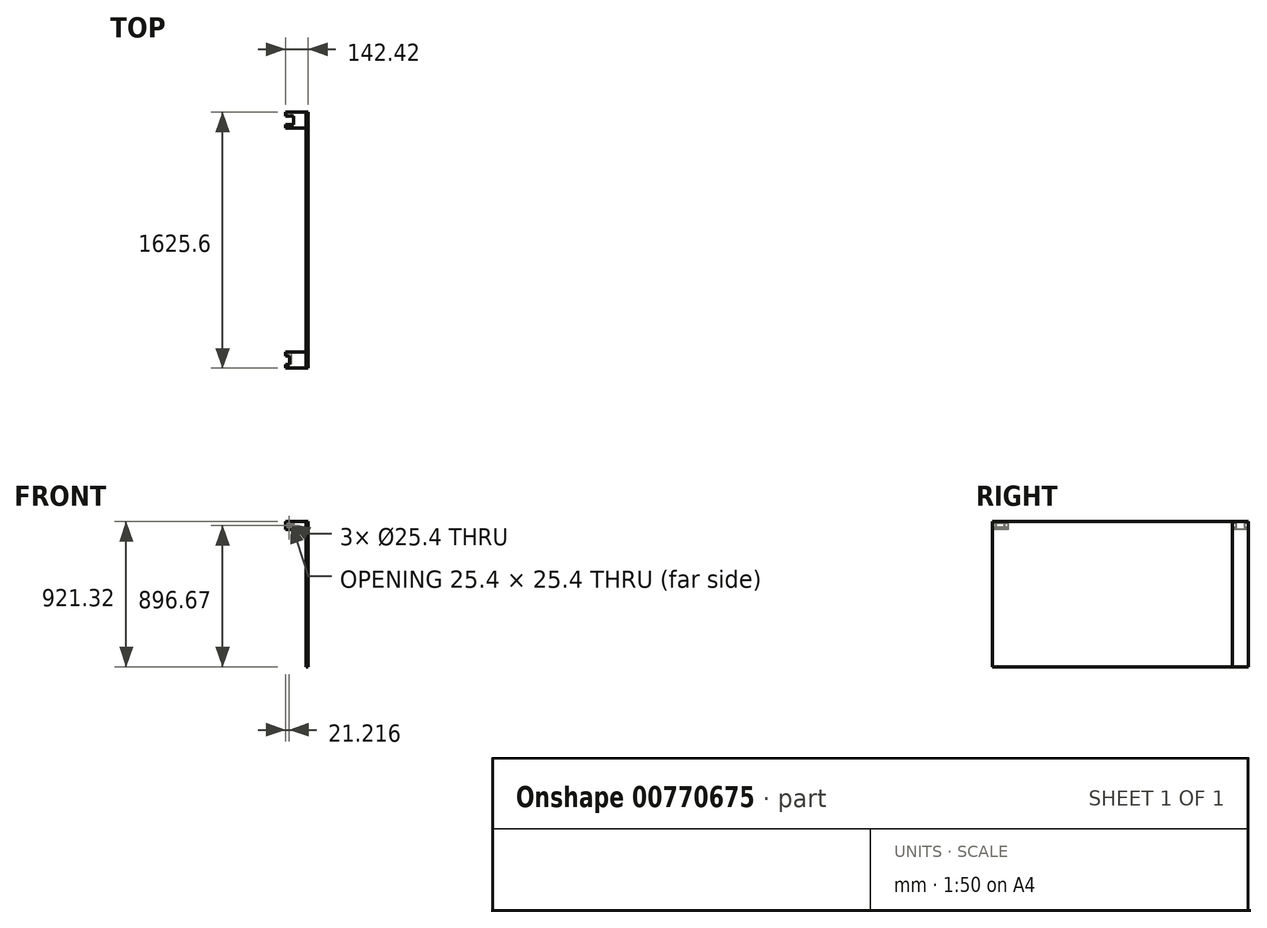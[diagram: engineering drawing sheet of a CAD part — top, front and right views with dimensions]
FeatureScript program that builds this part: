
annotation { "Feature Type Name" : "Feature", "Feature Type Description" : "" }
export const myFeature = defineFeature(function(context is Context, id is Id, definition is map)
    precondition{}
    {
        {
            var Q0;
            Q0=qCreatedBy(makeId("Front.planeOp"),FACE);
            var sketch = newSketch(context, id + "F0", { "sketchPlane" : qUnion([Q0])});
            skLineSegment(sketch, "E0.bottom", {"start": v(0, 0) * mm, "end": v(131.22, 0) * mm});
            skLineSegment(sketch, "E0.top", {"start": v(0, 48.37) * mm, "end": v(131.22, 48.37) * mm});
            skLineSegment(sketch, "E0.left", {"start": v(0, 0) * mm, "end": v(0, 48.37) * mm});
            skLineSegment(sketch, "E0.right", {"start": v(131.22, 0) * mm, "end": v(131.22, 48.37) * mm});
            skSolve(sketch);
        }
        {
            var Q0;
            Q0=makeQuery(id+"F0.imprint","IMPRINT",FACE,{"disambiguationData":[TD([[makeQuery(id+"F0.imprint","IMPRINT",EDGE,{"derivedFrom":sQuery(id+"F0.wireOp",EDGE,"E0.bottom")}),1.0]])]});
            extrude(context, id + "F1", {"entities" : qUnion([Q0]), "oppositeDirection" : true, "depth" : 101.6 * mm, "offsetDistance" : 25.4 * mm});
        }
        {
            var Q0;
            Q0=makeQuery(id+"F1.opExtrude","CAP_FACE",FACE,{"disambiguationData":[OSD([sQuery(id+"F0.wireOp",EDGE,"E0.bottom"),sQuery(id+"F0.wireOp",EDGE,"E0.top"),sQuery(id+"F0.wireOp",EDGE,"E0.left"),sQuery(id+"F0.wireOp",EDGE,"E0.right")])],"isStart":true});
            var sketch = newSketch(context, id + "F2", { "sketchPlane" : qUnion([Q0])});
            skLineSegment(sketch, "E1.bottom", {"start": v(131.22, 48.37) * mm, "end": v(142.42, 48.37) * mm});
            skLineSegment(sketch, "E1.top", {"start": v(131.22, -872.95) * mm, "end": v(142.42, -872.95) * mm});
            skLineSegment(sketch, "E1.left", {"start": v(131.22, 48.37) * mm, "end": v(131.22, -872.95) * mm});
            skLineSegment(sketch, "E1.right", {"start": v(142.42, 48.37) * mm, "end": v(142.42, -872.95) * mm});
            skSolve(sketch);
        }
        {
            var Q0;
            Q0 = qSketchRegion(id + "F2", true);
            extrude(context, id + "F3", {"entities" : qUnion([Q0]), "depth" : 1524 * mm, "offsetDistance" : 25.4 * mm});
        }
        {
            var Q0;
            Q0=makeQuery(id+"F3.opExtrude","CAP_FACE",FACE,{"disambiguationData":[OSD([sQuery(id+"F2.wireOp",EDGE,"E1.bottom"),sQuery(id+"F2.wireOp",EDGE,"E1.top"),sQuery(id+"F2.wireOp",EDGE,"E1.left"),sQuery(id+"F2.wireOp",EDGE,"E1.right")])],"isStart":true});
            extrude(context, id + "F4", {"entities" : qUnion([Q0]), "operationType" : NewBodyOperationType.ADD, "oppositeDirection" : true, "depth" : 101.6 * mm, "offsetDistance" : 25.4 * mm});
        }
        {
            var Q0;
            Q0=makeQuery(id+"F3.opExtrude","CAP_FACE",FACE,{"disambiguationData":[OSD([sQuery(id+"F2.wireOp",EDGE,"E1.bottom"),sQuery(id+"F2.wireOp",EDGE,"E1.top"),sQuery(id+"F2.wireOp",EDGE,"E1.left"),sQuery(id+"F2.wireOp",EDGE,"E1.right")])],"isStart":true});
            extrude(context, id + "F5", {"entities" : qUnion([Q0]), "depth" : 101.6 * mm, "offsetDistance" : 25.4 * mm});
        }
        {
            var Q0;
            Q0=makeQuery(id+"F3.opExtrude","CAP_FACE",FACE,{"disambiguationData":[OSD([sQuery(id+"F2.wireOp",EDGE,"E1.bottom"),sQuery(id+"F2.wireOp",EDGE,"E1.top"),sQuery(id+"F2.wireOp",EDGE,"E1.left"),sQuery(id+"F2.wireOp",EDGE,"E1.right")])],"isStart":false});
            var sketch = newSketch(context, id + "F6", { "sketchPlane" : qUnion([Q0])});
            skLineSegment(sketch, "E2.bottom", {"start": v(131.22, 48.37) * mm, "end": v(0, 48.37) * mm});
            skLineSegment(sketch, "E2.top", {"start": v(131.22, 0) * mm, "end": v(0, 0) * mm});
            skLineSegment(sketch, "E2.left", {"start": v(131.22, 48.37) * mm, "end": v(131.22, 0) * mm});
            skLineSegment(sketch, "E2.right", {"start": v(0, 48.37) * mm, "end": v(0, 0) * mm});
            skSolve(sketch);
        }
        {
            var Q0;
            Q0=makeQuery(id+"F6.imprint","IMPRINT",FACE,{"disambiguationData":[TD([[makeQuery(id+"F6.imprint","IMPRINT",EDGE,{"derivedFrom":sQuery(id+"F6.wireOp",EDGE,"E2.bottom")}),1.0]])]});
            extrude(context, id + "F7", {"entities" : qUnion([Q0]), "oppositeDirection" : true, "depth" : 101.6 * mm, "offsetDistance" : 25.4 * mm});
        }
        {
            var Q0;
            Q0=makeQuery(id+"F7.opExtrude","SWEPT_FACE",FACE,{"disambiguationData":[OSD([sQuery(id+"F6.wireOp",EDGE,"E2.right")])]});
            var sketch = newSketch(context, id + "F8", { "sketchPlane" : qUnion([Q0])});
            skLineSegment(sketch, "E3.bottom", {"start": v(1422.4, 48.37) * mm, "end": v(1446.74, 48.37) * mm});
            skLineSegment(sketch, "E3.top", {"start": v(1422.4, 0) * mm, "end": v(1446.74, 0) * mm});
            skLineSegment(sketch, "E3.left", {"start": v(1422.4, 48.37) * mm, "end": v(1422.4, 0) * mm});
            skLineSegment(sketch, "E3.right", {"start": v(1446.74, 48.37) * mm, "end": v(1446.74, 0) * mm});
            skLineSegment(sketch, "E4.bottom", {"start": v(1524, 48.37) * mm, "end": v(1499.82, 48.37) * mm});
            skLineSegment(sketch, "E4.top", {"start": v(1524, 0) * mm, "end": v(1499.82, 0) * mm});
            skLineSegment(sketch, "E4.left", {"start": v(1524, 48.37) * mm, "end": v(1524, 0) * mm});
            skLineSegment(sketch, "E4.right", {"start": v(1499.82, 48.37) * mm, "end": v(1499.82, 0) * mm});
            skLineSegment(sketch, "E5.bottom", {"start": v(1446.74, 48.37) * mm, "end": v(1499.82, 48.37) * mm});
            skLineSegment(sketch, "E5.top", {"start": v(1446.74, 0) * mm, "end": v(1499.82, 0) * mm});
            skSolve(sketch);
        }
        {
            var Q0;
            Q0=makeQuery(id+"F8.imprint","IMPRINT",FACE,{"disambiguationData":[TD([[makeQuery(id+"F8.imprint","IMPRINT",EDGE,{"derivedFrom":sQuery(id+"F8.wireOp",EDGE,"E5.bottom")}),-1.0]])]});
            extrude(context, id + "F9", {"entities" : qUnion([Q0]), "operationType" : NewBodyOperationType.REMOVE, "oppositeDirection" : true, "depth" : 25.4 * mm, "offsetDistance" : 25.4 * mm});
        }
        {
            var Q0;
            Q0=makeQuery(id+"F7.opExtrude","CAP_FACE",FACE,{"disambiguationData":[OSD([sQuery(id+"F6.wireOp",EDGE,"E2.bottom"),sQuery(id+"F6.wireOp",EDGE,"E2.top"),sQuery(id+"F6.wireOp",EDGE,"E2.left"),sQuery(id+"F6.wireOp",EDGE,"E2.right")])],"isStart":true});
            var sketch = newSketch(context, id + "F10", { "sketchPlane" : qUnion([Q0])});
            skCircle(sketch, "E6", {"center": v(21.22, 23.72) * mm, "radius": 21.22 * mm});
            skSolve(sketch);
        }
        {
            var Q0;
            Q0=sQuery(id+"F10.wireOp",VERTEX,"E6.center");
            var Q1;
            Q1=makeQuery(id+"F7.opExtrude","SWEPT_BODY",BODY,{"disambiguationData":[OSD([sQuery(id+"F6.wireOp",EDGE,"E2.bottom"),sQuery(id+"F6.wireOp",EDGE,"E2.top"),sQuery(id+"F6.wireOp",EDGE,"E2.left"),sQuery(id+"F6.wireOp",EDGE,"E2.right")])]});
            var Q2;
            Q2=makeQuery(id+"F1.opExtrude","SWEPT_BODY",BODY,{"disambiguationData":[OSD([sQuery(id+"F0.wireOp",EDGE,"E0.bottom"),sQuery(id+"F0.wireOp",EDGE,"E0.top"),sQuery(id+"F0.wireOp",EDGE,"E0.left"),sQuery(id+"F0.wireOp",EDGE,"E0.right")])]});
            hole(context, id + "F11", {"style" : HoleStyle.SIMPLE, "endStyle" : HoleEndStyle.THROUGH, "holeDiameter" : 25.4 * mm, "majorDiameter" : 6.35 * mm, "isTappedThrough" : true, "tappedDepth" : 12.7 * mm, "tapClearance" : 3, "locations" : qUnion([Q0]), "scope" : qUnion([Q1, Q2])});
        }
        {
            var Q0;
            Q0=makeQuery(id+"F1.opExtrude","SWEPT_FACE",FACE,{"disambiguationData":[OSD([sQuery(id+"F0.wireOp",EDGE,"E0.left")])]});
            var sketch = newSketch(context, id + "F12", { "sketchPlane" : qUnion([Q0])});
            skLineSegment(sketch, "E7.bottom", {"start": v(-101.6, 48.37) * mm, "end": v(-77.94, 48.37) * mm});
            skLineSegment(sketch, "E7.top", {"start": v(-101.6, 0) * mm, "end": v(-77.94, 0) * mm});
            skLineSegment(sketch, "E7.left", {"start": v(-101.6, 48.37) * mm, "end": v(-101.6, 0) * mm});
            skLineSegment(sketch, "E7.right", {"start": v(-77.94, 48.37) * mm, "end": v(-77.94, 0) * mm});
            skLineSegment(sketch, "E8.bottom", {"start": v(0, 48.37) * mm, "end": v(-24.49, 48.37) * mm});
            skLineSegment(sketch, "E8.top", {"start": v(0, 0) * mm, "end": v(-24.49, 0) * mm});
            skLineSegment(sketch, "E8.left", {"start": v(0, 48.37) * mm, "end": v(0, 0) * mm});
            skLineSegment(sketch, "E8.right", {"start": v(-24.49, 48.37) * mm, "end": v(-24.49, 0) * mm});
            skLineSegment(sketch, "E9.bottom", {"start": v(-77.94, 48.37) * mm, "end": v(-24.49, 48.37) * mm});
            skLineSegment(sketch, "E9.top", {"start": v(-77.94, 0) * mm, "end": v(-24.49, 0) * mm});
            skSolve(sketch);
        }
        {
            var Q0;
            Q0=makeQuery(id+"F12.imprint","IMPRINT",FACE,{"disambiguationData":[TD([[makeQuery(id+"F12.imprint","IMPRINT",EDGE,{"derivedFrom":sQuery(id+"F12.wireOp",EDGE,"E9.bottom")}),-1.0]])]});
            extrude(context, id + "F13", {"entities" : qUnion([Q0]), "operationType" : NewBodyOperationType.REMOVE, "oppositeDirection" : true, "depth" : 50.8 * mm, "offsetDistance" : 25.4 * mm});
        }
    });
